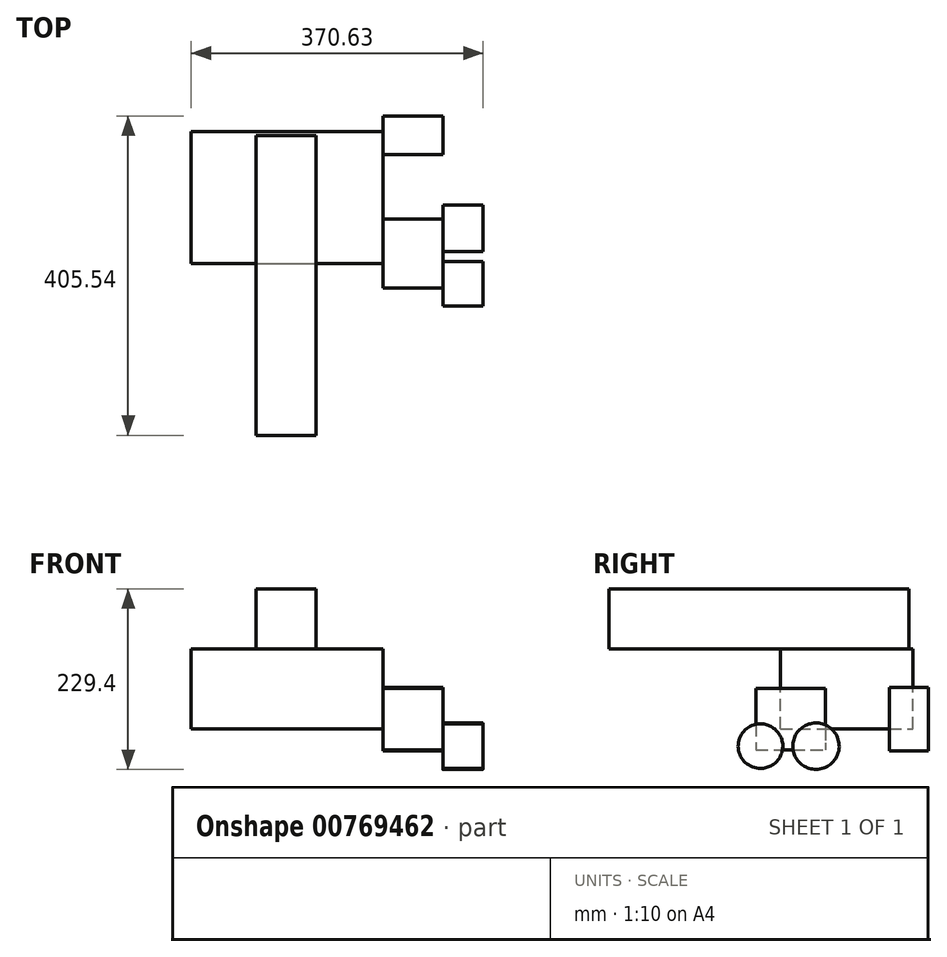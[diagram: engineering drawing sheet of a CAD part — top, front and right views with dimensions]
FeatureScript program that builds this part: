
annotation { "Feature Type Name" : "Feature", "Feature Type Description" : "" }
export const myFeature = defineFeature(function(context is Context, id is Id, definition is map)
    precondition{}
    {
        {
            var Q0;
            Q0=qCreatedBy(makeId("Front.planeOp"),FACE);
            var sketch = newSketch(context, id + "F0", { "sketchPlane" : qUnion([Q0])});
            skLineSegment(sketch, "E0.bottom", {"start": v(32.96, 86.24) * mm, "end": v(-43.24, 86.24) * mm});
            skLineSegment(sketch, "E0.top", {"start": v(32.96, 10.04) * mm, "end": v(-43.24, 10.04) * mm});
            skLineSegment(sketch, "E0.left", {"start": v(32.96, 86.24) * mm, "end": v(32.96, 10.04) * mm});
            skLineSegment(sketch, "E0.right", {"start": v(-43.24, 86.24) * mm, "end": v(-43.24, 10.04) * mm});
            skPoint(sketch, "E0.middle", {"position": v(-5.14, 48.14) * mm});
            skSolve(sketch);
        }
        {
            var Q0;
            Q0 = qSketchRegion(id + "F0", true);
            extrude(context, id + "F1", {"entities" : qUnion([Q0]), "depth" : 381 * mm, "offsetDistance" : 25.4 * mm});
        }
        {
            var Q0;
            Q0=makeQuery(id+"F1.opExtrude","CAP_FACE",FACE,{"disambiguationData":[OSD([sQuery(id+"F0.wireOp",EDGE,"E0.bottom"),sQuery(id+"F0.wireOp",EDGE,"E0.top"),sQuery(id+"F0.wireOp",EDGE,"E0.left"),sQuery(id+"F0.wireOp",EDGE,"E0.right")])],"isStart":false});
            var sketch = newSketch(context, id + "F2", { "sketchPlane" : qUnion([Q0])});
            skCircle(sketch, "E1", {"center": v(-27.06, 68.39) * mm, "radius": 12.7 * mm});
            skCircle(sketch, "E2", {"center": v(12.76, 72.7) * mm, "radius": 12.7 * mm});
            skCircle(sketch, "E3", {"center": v(-7.15, 31.06) * mm, "radius": 19.05 * mm});
            skSolve(sketch);
        }
        {
            var Q0;
            Q0=sQuery(id+"F2.wireOp",EDGE,"E3");
            extrude(context, id + "F3", {"bodyType" : ToolBodyType.SURFACE, "surfaceEntities" : qUnion([Q0]), "depth" : 76.2 * mm, "offsetDistance" : 25.4 * mm});
        }
        {
            var Q0;
            Q0=makeQuery(id+"F1.opExtrude","SWEPT_FACE",FACE,{"disambiguationData":[OSD([sQuery(id+"F0.wireOp",EDGE,"E0.top")])]});
            var sketch = newSketch(context, id + "F4", { "sketchPlane" : qUnion([Q0])});
            skLineSegment(sketch, "E4.bottom", {"start": v(-125.7, 162.99) * mm, "end": v(117.93, 162.99) * mm});
            skLineSegment(sketch, "E4.top", {"start": v(-125.7, -5.18) * mm, "end": v(117.93, -5.18) * mm});
            skLineSegment(sketch, "E4.left", {"start": v(-125.7, 162.99) * mm, "end": v(-125.7, -5.18) * mm});
            skLineSegment(sketch, "E4.right", {"start": v(117.93, 162.99) * mm, "end": v(117.93, -5.18) * mm});
            skPoint(sketch, "E4.middle", {"position": v(-3.89, 78.9) * mm});
            skSolve(sketch);
        }
        {
            var Q0;
            Q0 = qSketchRegion(id + "F4", true);
            extrude(context, id + "F5", {"entities" : qUnion([Q0]), "operationType" : NewBodyOperationType.ADD, "depth" : 101.6 * mm, "offsetDistance" : 25.4 * mm});
        }
        {
            var Q0;
            Q0=makeQuery(id+"F5.opExtrude","SWEPT_FACE",FACE,{"disambiguationData":[OSD([sQuery(id+"F4.wireOp",EDGE,"E4.right")])]});
            var sketch = newSketch(context, id + "F6", { "sketchPlane" : qUnion([Q0])});
            skLineSegment(sketch, "E5.bottom", {"start": v(-194.16, -40.55) * mm, "end": v(-105.96, -40.55) * mm});
            skLineSegment(sketch, "E5.top", {"start": v(-194.16, -118.2) * mm, "end": v(-105.96, -118.2) * mm});
            skLineSegment(sketch, "E5.left", {"start": v(-194.16, -40.55) * mm, "end": v(-194.16, -118.2) * mm});
            skLineSegment(sketch, "E5.right", {"start": v(-105.96, -40.55) * mm, "end": v(-105.96, -118.2) * mm});
            skPoint(sketch, "E5.middle", {"position": v(-150.06, -79.37) * mm});
            skLineSegment(sketch, "E6.bottom", {"start": v(-24.54, -39.04) * mm, "end": v(24.54, -39.04) * mm});
            skLineSegment(sketch, "E6.top", {"start": v(-24.54, -119.7) * mm, "end": v(24.54, -119.7) * mm});
            skLineSegment(sketch, "E6.left", {"start": v(-24.54, -39.04) * mm, "end": v(-24.54, -119.7) * mm});
            skLineSegment(sketch, "E6.right", {"start": v(24.54, -39.04) * mm, "end": v(24.54, -119.7) * mm});
            skPoint(sketch, "E6.middle", {"position": v(0, -79.37) * mm});
            skPoint(sketch, "E6.middle.positionSnap0", {"position": v(-105.96, -79.37) * mm});
            skPoint(sketch, "E6.centerSnap0", {"position": v(-105.96, -79.37) * mm});
            skSolve(sketch);
        }
        {
            var Q0;
            Q0 = qSketchRegion(id + "F6", true);
            extrude(context, id + "F7", {"entities" : qUnion([Q0]), "operationType" : NewBodyOperationType.ADD, "depth" : 76.2 * mm, "offsetDistance" : 25.4 * mm});
        }
        {
            var Q0;
            Q0=makeQuery(id+"F7.opExtrude","CAP_FACE",FACE,{"disambiguationData":[OSD([sQuery(id+"F6.wireOp",EDGE,"E5.bottom"),sQuery(id+"F6.wireOp",EDGE,"E5.top"),sQuery(id+"F6.wireOp",EDGE,"E5.left"),sQuery(id+"F6.wireOp",EDGE,"E5.right")])],"isStart":false});
            var sketch = newSketch(context, id + "F8", { "sketchPlane" : qUnion([Q0])});
            skCircle(sketch, "E7", {"center": v(-188.5, -113.67) * mm, "radius": 28.33 * mm});
            skCircle(sketch, "E8", {"center": v(-118.02, -113.67) * mm, "radius": 29.49 * mm});
            skSolve(sketch);
        }
        {
            var Q0;
            Q0 = qSketchRegion(id + "F8", true);
            extrude(context, id + "F9", {"entities" : qUnion([Q0]), "operationType" : NewBodyOperationType.ADD, "depth" : 50.8 * mm, "offsetDistance" : 25.4 * mm});
        }
    });
